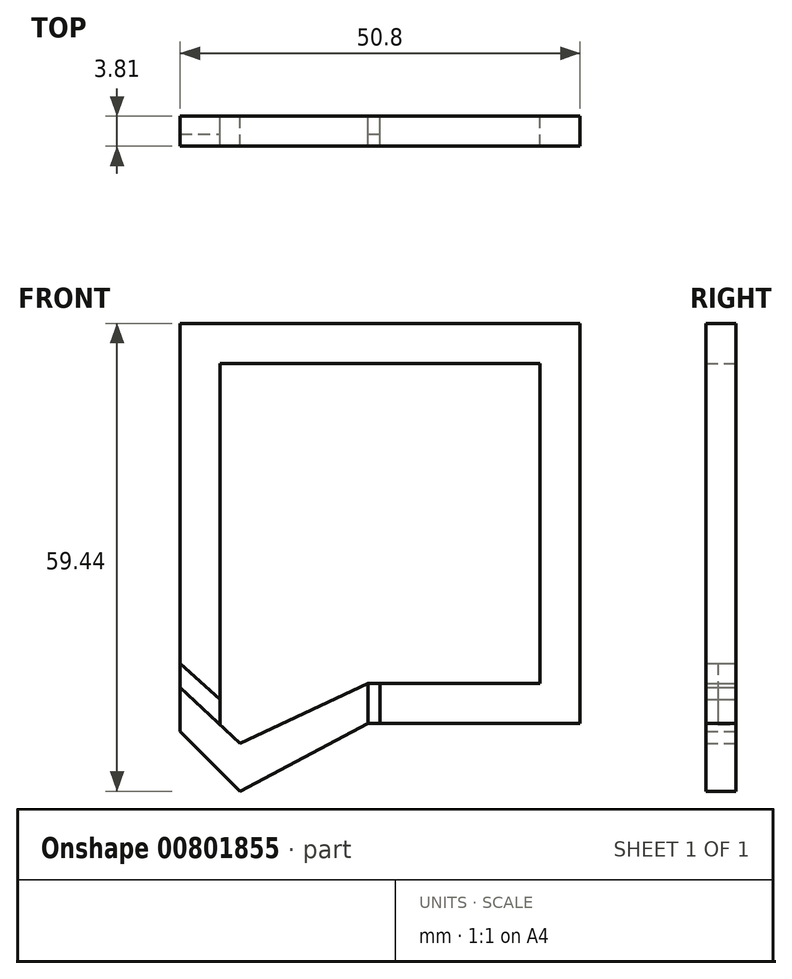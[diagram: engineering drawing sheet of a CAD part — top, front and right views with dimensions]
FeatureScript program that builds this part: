
annotation { "Feature Type Name" : "Feature", "Feature Type Description" : "" }
export const myFeature = defineFeature(function(context is Context, id is Id, definition is map)
    precondition{}
    {
        {
            var Q0;
            Q0=qCreatedBy(makeId("Front.planeOp"),FACE);
            var sketch = newSketch(context, id + "F0", { "sketchPlane" : qUnion([Q0])});
            skLineSegment(sketch, "E0", {"start": v(-25.4, 29.72) * mm, "end": v(25.4, 29.72) * mm});
            skLineSegment(sketch, "E1", {"start": v(25.4, 29.72) * mm, "end": v(25.4, -21.08) * mm});
            skLineSegment(sketch, "E2", {"start": v(-20.32, 24.64) * mm, "end": v(20.32, 24.64) * mm});
            skLineSegment(sketch, "E3", {"start": v(20.32, 24.64) * mm, "end": v(20.32, -16) * mm});
            skLineSegment(sketch, "E4", {"start": v(0, -16) * mm, "end": v(0, -21.08) * mm});
            skLineSegment(sketch, "E5", {"start": v(20.32, -16) * mm, "end": v(0, -16) * mm});
            skLineSegment(sketch, "E6", {"start": v(25.4, -21.08) * mm, "end": v(0, -21.08) * mm});
            skLineSegment(sketch, "E7", {"start": v(-1.52, -16) * mm, "end": v(-1.52, -21.08) * mm});
            skLineSegment(sketch, "E8", {"start": v(-17.78, -23.62) * mm, "end": v(-1.52, -16) * mm});
            skLineSegment(sketch, "E9", {"start": v(-17.78, -29.72) * mm, "end": v(-1.52, -21.08) * mm});
            skLineSegment(sketch, "E10", {"start": v(-25.4, -22.1) * mm, "end": v(-17.78, -29.72) * mm});
            skLineSegment(sketch, "E11", {"start": v(-25.4, -16.51) * mm, "end": v(-17.78, -23.62) * mm});
            skLineSegment(sketch, "E12", {"start": v(-25.4, -16.51) * mm, "end": v(-25.4, -22.1) * mm});
            skLineSegment(sketch, "E13", {"start": v(-25.4, -13.46) * mm, "end": v(-25.4, 29.72) * mm});
            skLineSegment(sketch, "E14", {"start": v(-20.32, -18.03) * mm, "end": v(-20.32, 24.64) * mm});
            skLineSegment(sketch, "E15", {"start": v(-25.4, -13.46) * mm, "end": v(-20.32, -18.03) * mm});
            skLineSegment(sketch, "E16", {"start": v(-25.4, -13.46) * mm, "end": v(-25.4, -16.51) * mm});
            skLineSegment(sketch, "E17", {"start": v(-20.32, -18.03) * mm, "end": v(-20.32, -21.25) * mm});
            skLineSegment(sketch, "E18", {"start": v(-1.52, -16) * mm, "end": v(0, -16) * mm});
            skLineSegment(sketch, "E19", {"start": v(-1.52, -21.08) * mm, "end": v(0, -21.08) * mm});
            skSolve(sketch);
        }
        {
            var Q0;
            Q0=makeQuery(id+"F0.imprint","IMPRINT",FACE,{"disambiguationData":[TD([[makeQuery(id+"F0.imprint","IMPRINT",EDGE,{"derivedFrom":sQuery(id+"F0.wireOp",EDGE,"E0")}),-1.0]])]});
            var Q1;
            Q1=makeQuery(id+"F0.imprint","IMPRINT",FACE,{"disambiguationData":[TD([[makeQuery(id+"F0.imprint","IMPRINT",EDGE,{"derivedFrom":sQuery(id+"F0.wireOp",EDGE,"E7")}),-1.0]])]});
            extrude(context, id + "F1", {"entities" : qUnion([Q0, Q1]), "depth" : 3.8 * mm, "offsetDistance" : 25.4 * mm});
        }
        {
            var Q0;
            Q0=makeQuery(id+"F0.imprint","IMPRINT",FACE,{"disambiguationData":[TD([[makeQuery(id+"F0.imprint","IMPRINT",EDGE,{"derivedFrom":sQuery(id+"F0.wireOp",EDGE,"E15")}),-1.0]])]});
            var Q1;
            Q1=makeQuery(id+"F0.imprint","IMPRINT",FACE,{"disambiguationData":[TD([[makeQuery(id+"F0.imprint","IMPRINT",EDGE,{"derivedFrom":sQuery(id+"F0.wireOp",EDGE,"E4")}),-1.0]])]});
            extrude(context, id + "F2", {"entities" : qUnion([Q0, Q1]), "depth" : 2.3 * mm, "offsetDistance" : 25.4 * mm});
        }
    });
